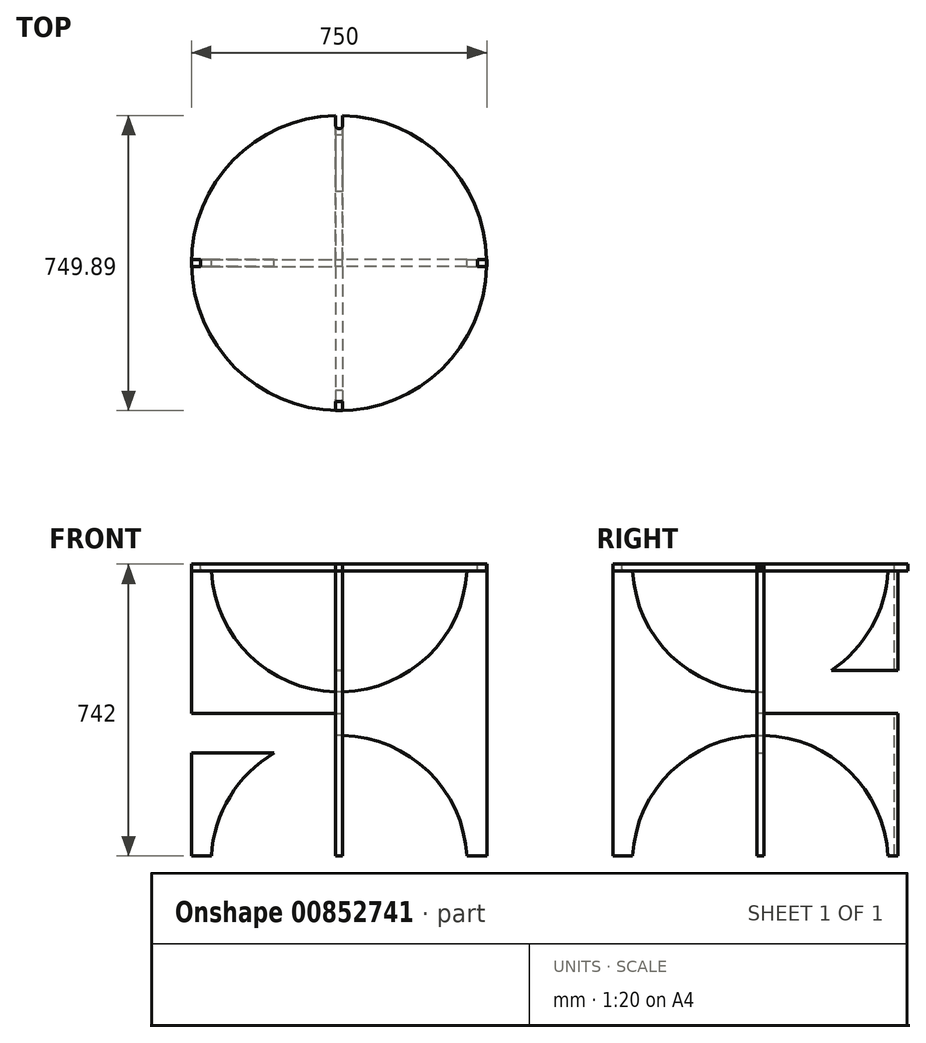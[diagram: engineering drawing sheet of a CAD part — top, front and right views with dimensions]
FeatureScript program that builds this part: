
annotation { "Feature Type Name" : "Feature", "Feature Type Description" : "" }
export const myFeature = defineFeature(function(context is Context, id is Id, definition is map)
    precondition{}
    {
        {
            var Q0;
            Q0=qCreatedBy(makeId("Front.planeOp"),FACE);
            var sketch = newSketch(context, id + "F0", { "sketchPlane" : qUnion([Q0])});
            skLineSegment(sketch, "E0.bottom", {"start": v(-375, -190) * mm, "end": v(140, -190) * mm});
            skLineSegment(sketch, "E0.top", {"start": v(-375, 190) * mm, "end": v(-352, 190) * mm});
            skLineSegment(sketch, "E0.left", {"start": v(-375, -190) * mm, "end": v(-375, 190) * mm});
            skLineSegment(sketch, "E0.right", {"start": v(375, -190) * mm, "end": v(375, 190) * mm});
            skPoint(sketch, "E0.middle", {"position": v(0, 0) * mm});
            skArc(sketch, "E1", {"start": v(-324.5, 172) * mm, "mid": v(0, -135) * mm, "end": v(324.5, 172) * mm});
            skLineSegment(sketch, "E2.trimOffspring", {"start": v(352, 190) * mm, "end": v(375, 190) * mm});
            skLineSegment(sketch, "E3.trimOffspring", {"start": v(140, -190) * mm, "end": v(375, -190) * mm});
            skLineSegment(sketch, "E4.bottom", {"start": v(-352, 172) * mm, "end": v(-324.5, 172) * mm});
            skLineSegment(sketch, "E4.left", {"start": v(-352, 172) * mm, "end": v(-352, 190) * mm});
            skLineSegment(sketch, "E4.right", {"start": v(352, 172) * mm, "end": v(352, 190) * mm});
            skPoint(sketch, "E5.orphan", {"position": v(-352, 208) * mm});
            skLineSegment(sketch, "E6.trimOffspring", {"start": v(324.5, 172) * mm, "end": v(352, 172) * mm});
            skPoint(sketch, "E7.orphan", {"position": v(352, 208) * mm});
            skLineSegment(sketch, "E8.MirrorCS", {"start": v(324.5, -552) * mm, "end": v(352, -552) * mm});
            skLineSegment(sketch, "E9.MirrorCS", {"start": v(-352, -552) * mm, "end": v(-324.5, -552) * mm});
            skPoint(sketch, "E10.MirrorP", {"position": v(0, -380) * mm});
            skPoint(sketch, "E11.MirrorP", {"position": v(-352, -588) * mm});
            skPoint(sketch, "E12.MirrorP", {"position": v(0, -570) * mm});
            skPoint(sketch, "E13.MirrorP", {"position": v(352, -588) * mm});
            skArc(sketch, "E14.MirrorCS", {"start": v(-324.5, -552) * mm, "mid": v(0, -245) * mm, "end": v(324.5, -552) * mm});
            skLineSegment(sketch, "E15.MirrorCS", {"start": v(375, -190) * mm, "end": v(375, -552) * mm});
            skLineSegment(sketch, "E16.MirrorCS", {"start": v(-375, -190) * mm, "end": v(-375, -552) * mm});
            skLineSegment(sketch, "E17", {"start": v(-352, -552) * mm, "end": v(-375, -552) * mm});
            skLineSegment(sketch, "E18", {"start": v(352, -552) * mm, "end": v(375, -552) * mm});
            skPoint(sketch, "E19.orphan", {"position": v(-375, -570) * mm});
            skPoint(sketch, "E20.orphan", {"position": v(375, -570) * mm});
            skSolve(sketch);
        }
        {
            var Q0;
            Q0=qSketchRegion(id+"F0",true);
            extrude(context, id + "F1", {"entities" : qUnion([Q0]), "depth" : 9 * mm, "offsetDistance" : 25 * mm, "hasSecondDirection" : true, "secondDirectionOppositeDirection" : true, "secondDirectionDepth" : 9 * mm});
        }
        {
            var Q0;
            Q0=qCreatedBy(makeId("Right.planeOp"),FACE);
            var Q1;
            Q1=qCreatedBy(makeId("Front.planeOp"),FACE);
            cPlane(context, id + "F2", {"entities" : qUnion([Q0, Q1]), "cplaneType" : CPlaneType.MID_PLANE, "offset" : 25 * mm, "width" : 150 * mm, "height" : 150 * mm});
        }
        {
            var Q0;
            Q0=makeQuery(id+"F1.opExtrude","SWEPT_BODY",BODY,{"disambiguationData":[OSD([sQuery(id+"F0.wireOp",EDGE,"E0.bottom"),sQuery(id+"F0.wireOp",EDGE,"E0.top"),sQuery(id+"F0.wireOp",EDGE,"E0.left"),sQuery(id+"F0.wireOp",EDGE,"E0.right"),sQuery(id+"F0.wireOp",EDGE,"E1"),sQuery(id+"F0.wireOp",EDGE,"EXiE6QKu-Vo7E-oY48-lKYo-ds7yFPW4EHc2"),sQuery(id+"F0.wireOp",EDGE,"E2.trimOffspring"),sQuery(id+"F0.wireOp",EDGE,"E3.trimOffspring")])]});
            var Q1;
            Q1=qCreatedBy(id+"F2.planeOp",FACE);
            mirror(context, id + "F3", {"entities" : qUnion([Q0]), "mirrorPlane" : qUnion([Q1])});
        }
        {
            var Q0;
            Q0=makeQuery(id+"F1.opExtrude","SWEPT_FACE",FACE,{"disambiguationData":[OSD([sQuery(id+"F0.wireOp",EDGE,"E2.trimOffspring")])]});
            var sketch = newSketch(context, id + "F4", { "sketchPlane" : qUnion([Q0])});
            skCircle(sketch, "E21", {"center": v(0, 0) * mm, "radius": 375 * mm});
            skSolve(sketch);
        }
        {
            var Q0;
            {var subQ1=sQuery(id+"F0.wireOp",EDGE,"E2.trimOffspring");var subQ6=makeQuery(id+"F1.opExtrude","SWEPT_EDGE",EDGE,{"disambiguationData":[OSD([sQuery(id+"F0.wireOp",EDGE,"E1"),subQ1])]});Q0=makeQuery(id+"F4.imprint","IMPRINT",FACE,{"disambiguationData":[TD([[makeQuery(id+"F4.imprint","IMPRINT",EDGE,{"derivedFrom":subQ6}),1.0]])]});}
            var Q1;
            {var subQ1=sQuery(id+"F0.wireOp",EDGE,"E2.trimOffspring");var subQ6=makeQuery(id+"F1.opExtrude","SWEPT_EDGE",EDGE,{"disambiguationData":[OSD([subQ1,sQuery(id+"F0.wireOp",EDGE,"E4.right")])]});Q1=makeQuery(id+"F4.imprint","IMPRINT",FACE,{"disambiguationData":[TD([[makeQuery(id+"F4.imprint","IMPRINT",EDGE,{"derivedFrom":subQ6}),1.0]])]});}
            extrude(context, id + "F5", {"entities" : qUnion([Q0, Q1]), "oppositeDirection" : true, "depth" : 18 * mm, "offsetDistance" : 25 * mm});
        }
        {
            var Q0;
            Q0=makeQuery(id+"F5.opExtrude","CAP_FACE",FACE,{"disambiguationData":[OSD([sQuery(id+"F0.wireOp",EDGE,"E1"),sQuery(id+"F0.wireOp",EDGE,"E2.trimOffspring"),sQuery(id+"F4.wireOp",EDGE,"E21")])],"isStart":true});
            var sketch = newSketch(context, id + "F6", { "sketchPlane" : qUnion([Q0])});
            skLineSegment(sketch, "E22.top", {"start": v(9, 400) * mm, "end": v(-9, 400) * mm});
            skLineSegment(sketch, "E22.left", {"start": v(9, 350) * mm, "end": v(9, 400) * mm});
            skLineSegment(sketch, "E22.right", {"start": v(-9, 350) * mm, "end": v(-9, 400) * mm});
            skPoint(sketch, "E22.middle", {"position": v(0, 375) * mm});
            skArc(sketch, "E23", {"start": v(-9, 350) * mm, "mid": v(0, 341) * mm, "end": v(9, 350) * mm});
            skSolve(sketch);
        }
        {
            var Q0;
            Q0=qSketchRegion(id+"F6",true);
            extrude(context, id + "F7", {"entities" : qUnion([Q0]), "operationType" : NewBodyOperationType.REMOVE, "endBound" : BoundingType.THROUGH_ALL, "oppositeDirection" : true, "depth" : 25 * mm, "offsetDistance" : 25 * mm});
        }
        {
            var Q0;
            Q0=makeQuery(id+"F1.opExtrude","SWEPT_EDGE",EDGE,{"disambiguationData":[OSD([sQuery(id+"F0.wireOp",EDGE,"E4.bottom"),sQuery(id+"F0.wireOp",EDGE,"E4.left")])]});
            var Q1;
            Q1=makeQuery(id+"F3.opPattern","COPY",EDGE,{"derivedFrom":makeQuery(id+"F1.opExtrude","SWEPT_EDGE",EDGE,{"disambiguationData":[OSD([sQuery(id+"F0.wireOp",EDGE,"E4.bottom"),sQuery(id+"F0.wireOp",EDGE,"E4.left")])]}),"instanceName":"1"});
            var Q2;
            Q2=makeQuery(id+"F1.opExtrude","SWEPT_EDGE",EDGE,{"disambiguationData":[OSD([sQuery(id+"F0.wireOp",EDGE,"E4.right"),sQuery(id+"F0.wireOp",EDGE,"E6.trimOffspring")])]});
            var Q3;
            Q3=makeQuery(id+"F3.opPattern","COPY",EDGE,{"derivedFrom":makeQuery(id+"F1.opExtrude","SWEPT_EDGE",EDGE,{"disambiguationData":[OSD([sQuery(id+"F0.wireOp",EDGE,"E4.right"),sQuery(id+"F0.wireOp",EDGE,"E6.trimOffspring")])]}),"instanceName":"1"});
            fillet(context, id + "F8", {"entities" : qUnion([Q0, Q1, Q2, Q3]), "radius" : 5 * mm, "tangentPropagation" : true, "allowEdgeOverflow" : false});
        }
        {
            var Q0;
            {var subQ0=sQuery(id+"F0.wireOp",EDGE,"E2.trimOffspring");var subQ1=sQuery(id+"F0.wireOp",EDGE,"EXiE6QKu-Vo7E-oY48-lKYo-ds7yFPW4EHc2");var subQ3=sQuery(id+"F0.wireOp",EDGE,"E1");var subQ5=sQuery(id+"F0.wireOp",EDGE,"E0.right");var subQ6=sQuery(id+"F0.wireOp",EDGE,"E3.trimOffspring");var subQ7=makeQuery(id+"F1.opExtrude","CAP_FACE",FACE,{"disambiguationData":[OSD([sQuery(id+"F0.wireOp",EDGE,"E0.bottom"),sQuery(id+"F0.wireOp",EDGE,"E0.top"),sQuery(id+"F0.wireOp",EDGE,"E0.left"),subQ5,subQ3,subQ1,subQ0,subQ6])],"isStart":false});Q0=makeQuery(id+"F3.boolean.opBoolean","SPLIT",FACE,{"disambiguationData":[TD([makeQuery(id+"F1.opExtrude","SWEPT_FACE",FACE,{"disambiguationData":[OSD([subQ5])]})])],"derivedFrom":subQ7});}
            var sketch = newSketch(context, id + "F9", { "sketchPlane" : qUnion([Q0])});
            skLineSegment(sketch, "E24.bottom", {"start": v(9, -190) * mm, "end": v(-9, -190) * mm});
            skLineSegment(sketch, "E24.top", {"start": v(9, -80) * mm, "end": v(-9, -80) * mm});
            skLineSegment(sketch, "E24.left", {"start": v(9, -190) * mm, "end": v(9, -80) * mm});
            skLineSegment(sketch, "E24.right", {"start": v(-9, -190) * mm, "end": v(-9, -80) * mm});
            skPoint(sketch, "E24.middle", {"position": v(0, -135) * mm});
            skSolve(sketch);
        }
        {
            var Q0;
            Q0=qSketchRegion(id+"F9",true);
            extrude(context, id + "F10", {"entities" : qUnion([Q0]), "operationType" : NewBodyOperationType.REMOVE, "endBound" : BoundingType.THROUGH_ALL, "oppositeDirection" : true, "depth" : 25 * mm, "offsetDistance" : 25 * mm});
        }
        {
            var Q0;
            Q0=makeQuery(id+"F3.opPattern","COPY",FACE,{"derivedFrom":makeQuery(id+"F1.opExtrude","CAP_FACE",FACE,{"disambiguationData":[OSD([sQuery(id+"F0.wireOp",EDGE,"E0.bottom"),sQuery(id+"F0.wireOp",EDGE,"E0.top"),sQuery(id+"F0.wireOp",EDGE,"E0.left"),sQuery(id+"F0.wireOp",EDGE,"E0.right"),sQuery(id+"F0.wireOp",EDGE,"E1"),sQuery(id+"F0.wireOp",EDGE,"EXiE6QKu-Vo7E-oY48-lKYo-ds7yFPW4EHc2"),sQuery(id+"F0.wireOp",EDGE,"E2.trimOffspring"),sQuery(id+"F0.wireOp",EDGE,"E3.trimOffspring")])],"isStart":false}),"instanceName":"1"});
            var sketch = newSketch(context, id + "F11", { "sketchPlane" : qUnion([Q0])});
            skLineSegment(sketch, "E25.bottom", {"start": v(9, -290) * mm, "end": v(-9, -290) * mm});
            skLineSegment(sketch, "E25.top", {"start": v(9, -190) * mm, "end": v(-9, -190) * mm});
            skLineSegment(sketch, "E25.left", {"start": v(9, -290) * mm, "end": v(9, -190) * mm});
            skLineSegment(sketch, "E25.right", {"start": v(-9, -290) * mm, "end": v(-9, -190) * mm});
            skPoint(sketch, "E25.middle", {"position": v(0, -240) * mm});
            skSolve(sketch);
        }
        {
            var Q0;
            Q0=qSketchRegion(id+"F11",true);
            extrude(context, id + "F12", {"entities" : qUnion([Q0]), "operationType" : NewBodyOperationType.REMOVE, "endBound" : BoundingType.THROUGH_ALL, "oppositeDirection" : true, "depth" : 25 * mm, "offsetDistance" : 25 * mm});
        }
    });
